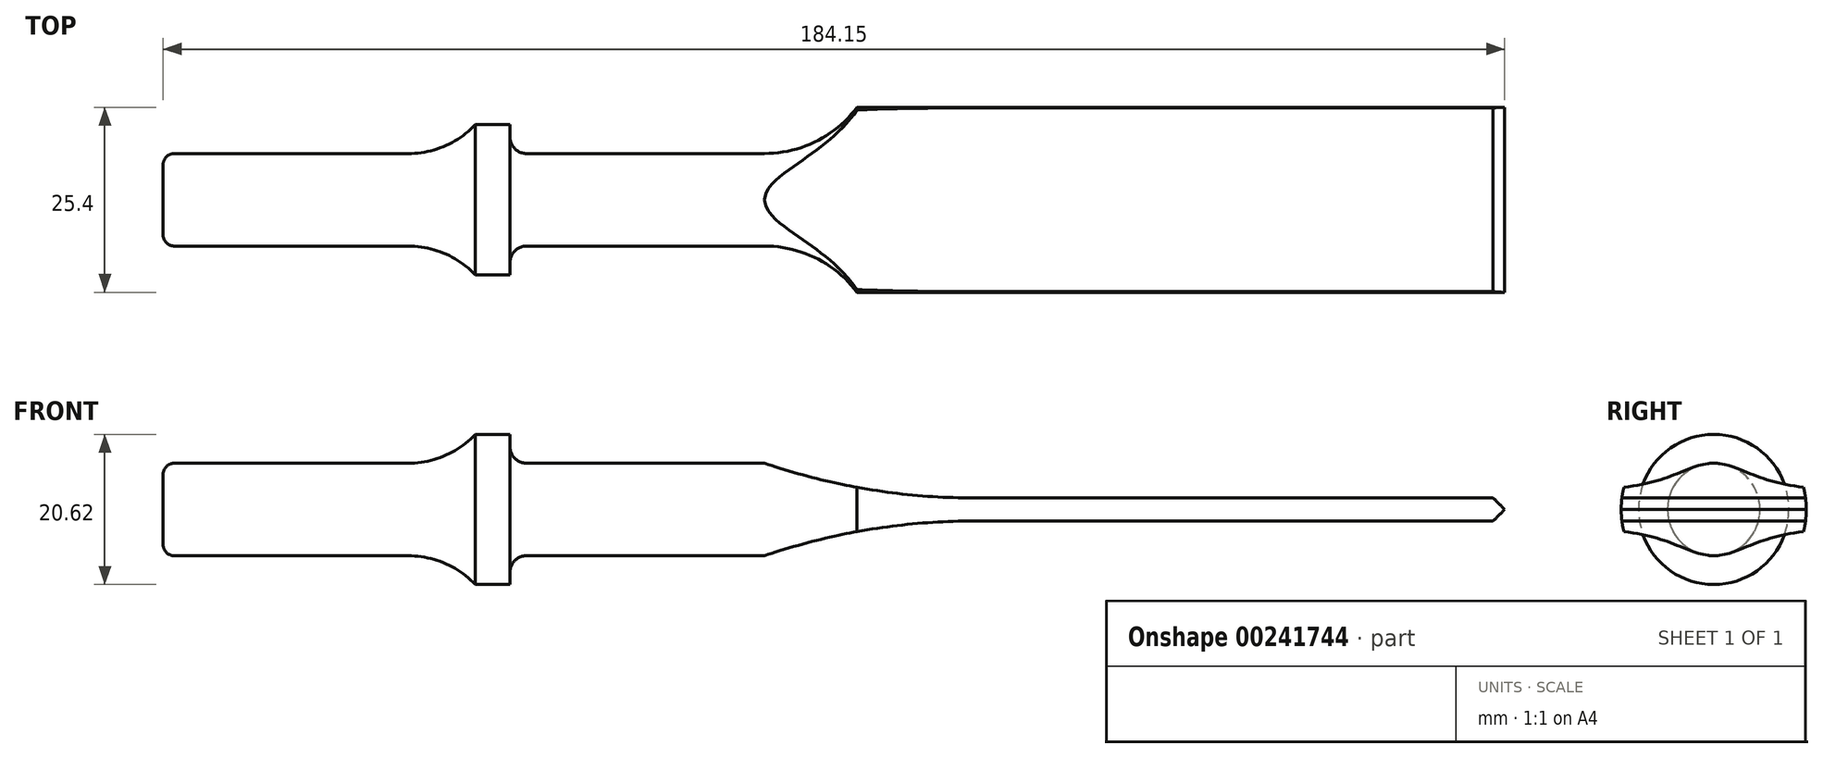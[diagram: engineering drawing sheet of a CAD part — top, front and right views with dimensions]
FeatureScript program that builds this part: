
annotation { "Feature Type Name" : "Feature", "Feature Type Description" : "" }
export const myFeature = defineFeature(function(context is Context, id is Id, definition is map)
    precondition{}
    {
        {
            var Q0;
            Q0=qCreatedBy(makeId("Front.planeOp"),FACE);
            var sketch = newSketch(context, id + "F0", { "sketchPlane" : qUnion([Q0])});
            skLineSegment(sketch, "E0", {"start": v(0, 0) * mm, "end": v(184.15, 0) * mm});
            skLineSegment(sketch, "E1", {"start": v(0, 0) * mm, "end": v(0, 4.83) * mm});
            skLineSegment(sketch, "E2", {"start": v(1.52, 6.35) * mm, "end": v(33.63, 6.35) * mm});
            skLineSegment(sketch, "E3", {"start": v(42.85, 10.31) * mm, "end": v(47.6, 10.31) * mm});
            skLineSegment(sketch, "E4", {"start": v(47.6, 10.31) * mm, "end": v(47.6, 8.64) * mm});
            skLineSegment(sketch, "E5", {"start": v(184.15, 12.7) * mm, "end": v(184.15, 0) * mm});
            skLineSegment(sketch, "E6.0", {"start": v(82.55, 6.35) * mm, "end": v(82.55, 0) * mm, "construction": true});
            skLineSegment(sketch, "E7.0", {"start": v(95.25, 12.7) * mm, "end": v(95.25, 0) * mm, "construction": true});
            skLineSegment(sketch, "E8", {"start": v(184.15, 12.7) * mm, "end": v(95.25, 12.7) * mm});
            skLineSegment(sketch, "E9.trimOffspring", {"start": v(49.89, 6.35) * mm, "end": v(82.55, 6.35) * mm});
            skArc(sketch, "E10", {"start": v(82.55, 6.35) * mm, "mid": v(89.65, 8.03) * mm, "end": v(95.25, 12.7) * mm});
            skArc(sketch, "E11", {"start": v(33.63, 6.35) * mm, "mid": v(38.65, 7.38) * mm, "end": v(42.85, 10.31) * mm});
            skPoint(sketch, "E12.visualSharp", {"position": v(0, 6.35) * mm});
            skArc(sketch, "E12.filletArc", {"start": v(1.52, 6.35) * mm, "mid": v(0.45, 5.9) * mm, "end": v(0, 4.83) * mm});
            skPoint(sketch, "E13.visualSharp", {"position": v(47.6, 6.35) * mm});
            skArc(sketch, "E13.filletArc", {"start": v(47.6, 8.64) * mm, "mid": v(48.27, 7.02) * mm, "end": v(49.89, 6.35) * mm});
            skSolve(sketch);
        }
        {
            var Q0;
            Q0=makeQuery(id+"F0.imprint","IMPRINT",FACE,{"disambiguationData":[TD([[makeQuery(id+"F0.imprint","IMPRINT",EDGE,{"derivedFrom":sQuery(id+"F0.wireOp",EDGE,"E0")}),1.0]])]});
            var Q1;
            Q1=sQuery(id+"F0.wireOp",EDGE,"E0");
            revolve(context, id + "F1", {"entities" : qUnion([Q0]), "axis" : qUnion([Q1]), "revolveType" : RevolveType.FULL});
        }
        {
            var Q0;
            Q0=qCreatedBy(makeId("Front.planeOp"),FACE);
            var sketch = newSketch(context, id + "F2", { "sketchPlane" : qUnion([Q0])});
            skLineSegment(sketch, "E14", {"start": v(0, 0) * mm, "end": v(184.15, 0) * mm, "construction": true});
            skLineSegment(sketch, "E15", {"start": v(184.15, 0) * mm, "end": v(184.15, 42.79) * mm, "construction": true});
            skLineSegment(sketch, "E16.0", {"start": v(82.55, 6.35) * mm, "end": v(82.55, 42.79) * mm, "construction": true});
            skLineSegment(sketch, "E17.0", {"start": v(0, 6.35) * mm, "end": v(184.15, 6.35) * mm, "construction": true});
            skLineSegment(sketch, "E18.0", {"start": v(111.26, 1.59) * mm, "end": v(182.56, 1.59) * mm});
            skPoint(sketch, "E19", {"position": v(82.55, 6.35) * mm});
            skArc(sketch, "E20", {"start": v(82.55, 6.35) * mm, "mid": v(96.7, 2.79) * mm, "end": v(111.26, 1.59) * mm});
            skLineSegment(sketch, "E21", {"start": v(82.55, 6.35) * mm, "end": v(82.55, 49.45) * mm});
            skLineSegment(sketch, "E22", {"start": v(82.55, 49.45) * mm, "end": v(191.21, 49.45) * mm});
            skLineSegment(sketch, "E23", {"start": v(184.15, 0) * mm, "end": v(182.56, 1.59) * mm});
            skLineSegment(sketch, "E24", {"start": v(191.21, 49.45) * mm, "end": v(184.15, 0) * mm});
            skLineSegment(sketch, "E25.MirrorCS", {"start": v(165.1, 0) * mm, "end": v(-19.05, 0) * mm, "construction": true});
            skLineSegment(sketch, "E26.MirrorCS", {"start": v(82.55, -6.35) * mm, "end": v(82.55, -42.79) * mm, "construction": true});
            skLineSegment(sketch, "E27.MirrorCS", {"start": v(82.55, -49.45) * mm, "end": v(191.21, -49.45) * mm});
            skLineSegment(sketch, "E28.MirrorCS", {"start": v(82.55, -6.35) * mm, "end": v(82.55, -49.45) * mm});
            skLineSegment(sketch, "E29.MirrorCS", {"start": v(191.21, -49.45) * mm, "end": v(184.15, 0) * mm});
            skLineSegment(sketch, "E30.MirrorCS", {"start": v(184.15, 0) * mm, "end": v(182.56, -1.59) * mm});
            skLineSegment(sketch, "E31.MirrorCS", {"start": v(111.26, -1.59) * mm, "end": v(182.56, -1.59) * mm});
            skArc(sketch, "E32.MirrorCS", {"start": v(82.55, -6.35) * mm, "mid": v(96.7, -2.79) * mm, "end": v(111.26, -1.59) * mm});
            skSolve(sketch);
        }
        {
            var Q0;
            Q0=makeQuery(id+"F2.imprint","IMPRINT",FACE,{"disambiguationData":[TD([[makeQuery(id+"F2.imprint","IMPRINT",EDGE,{"derivedFrom":sQuery(id+"F2.wireOp",EDGE,"E18.0")}),1.0]])]});
            var Q1;
            Q1=makeQuery(id+"F2.imprint","IMPRINT",FACE,{"disambiguationData":[TD([[makeQuery(id+"F2.imprint","IMPRINT",EDGE,{"derivedFrom":sQuery(id+"F2.wireOp",EDGE,"E27.MirrorCS")}),1.0]])]});
            extrude(context, id + "F3", {"entities" : qUnion([Q0, Q1]), "operationType" : NewBodyOperationType.REMOVE, "depth" : 48.5 * mm});
        }
        {
            var Q0;
            Q0 = qSketchRegion(id + "F2", true);
            extrude(context, id + "F4", {"entities" : qUnion([Q0]), "operationType" : NewBodyOperationType.REMOVE, "oppositeDirection" : true, "depth" : 25.4 * mm});
        }
    });
